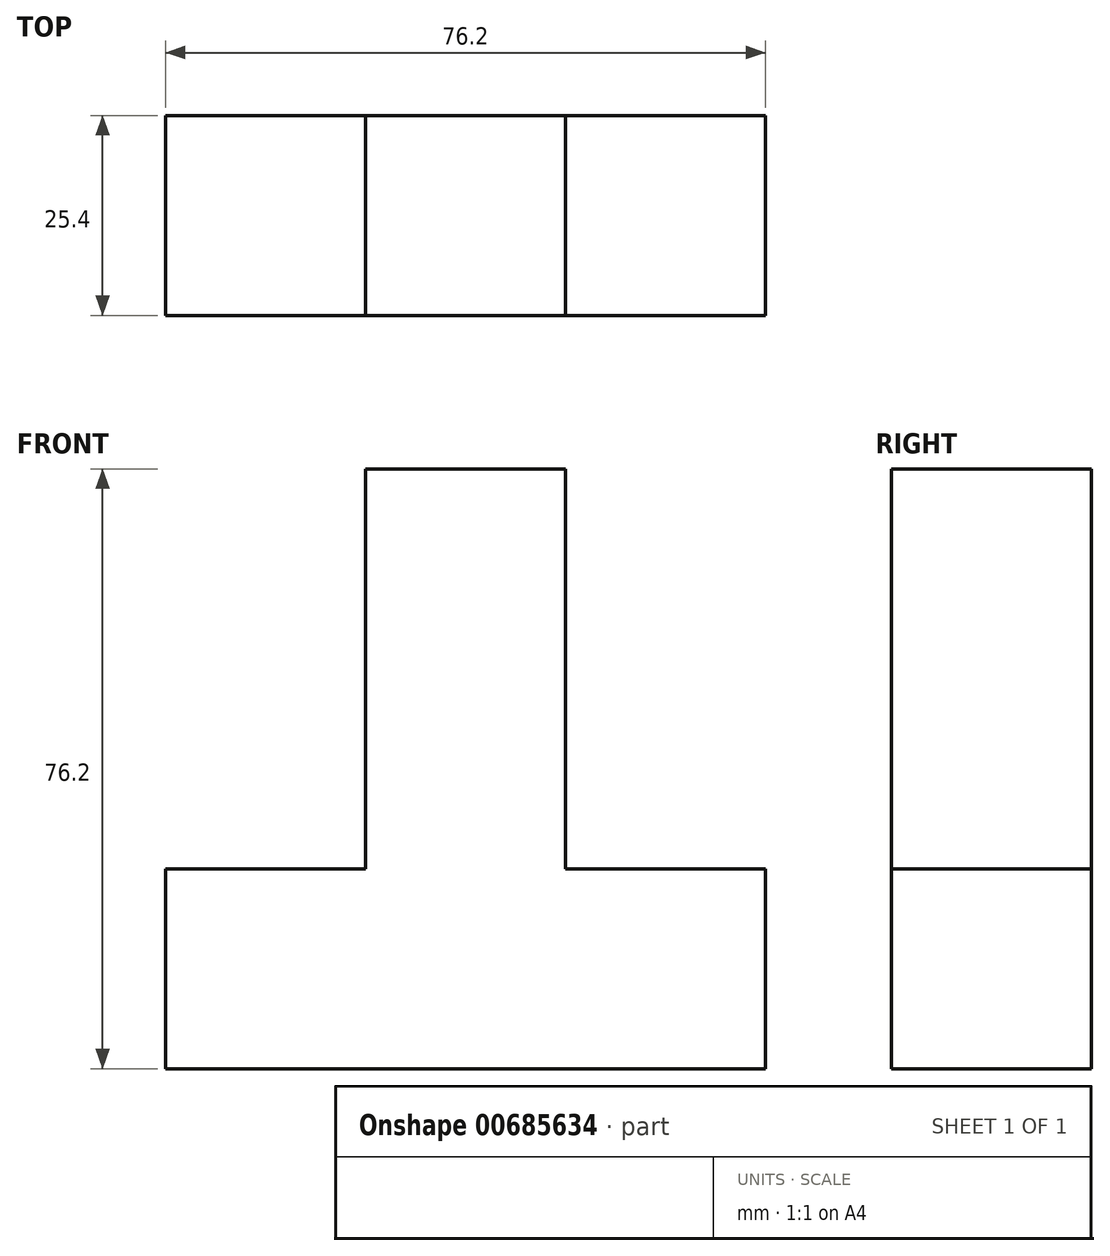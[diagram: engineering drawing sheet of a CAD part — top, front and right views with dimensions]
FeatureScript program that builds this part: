
annotation { "Feature Type Name" : "Feature", "Feature Type Description" : "" }
export const myFeature = defineFeature(function(context is Context, id is Id, definition is map)
    precondition{}
    {
        {
            var Q0;
            Q0=qCreatedBy(makeId("Front.planeOp"),FACE);
            var sketch = newSketch(context, id + "F0", { "sketchPlane" : qUnion([Q0])});
            skLineSegment(sketch, "E0", {"start": v(-61.4, -40.66) * mm, "end": v(14.8, -40.66) * mm});
            skLineSegment(sketch, "E1", {"start": v(14.8, -40.66) * mm, "end": v(14.8, -15.26) * mm});
            skLineSegment(sketch, "E2", {"start": v(14.8, -15.26) * mm, "end": v(-10.6, -15.26) * mm});
            skLineSegment(sketch, "E3", {"start": v(-10.6, -15.26) * mm, "end": v(-10.6, 35.54) * mm});
            skLineSegment(sketch, "E4", {"start": v(-10.6, 35.54) * mm, "end": v(-36, 35.54) * mm});
            skLineSegment(sketch, "E5", {"start": v(-36, 35.54) * mm, "end": v(-36, -15.26) * mm});
            skLineSegment(sketch, "E6", {"start": v(-36, -15.26) * mm, "end": v(-61.4, -15.26) * mm});
            skLineSegment(sketch, "E7", {"start": v(-61.4, -15.26) * mm, "end": v(-61.4, -40.66) * mm});
            skSolve(sketch);
        }
        {
            var Q0;
            Q0 = qSketchRegion(id + "F0", true);
            extrude(context, id + "F1", {"entities" : qUnion([Q0]), "depth" : 25.4 * mm, "offsetDistance" : 25.4 * mm});
        }
    });
